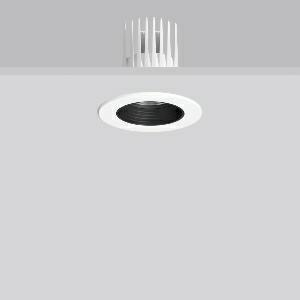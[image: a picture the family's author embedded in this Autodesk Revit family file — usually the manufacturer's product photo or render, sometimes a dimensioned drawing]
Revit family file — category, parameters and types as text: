
# Revit family: heledon_mini_e_901745_002_1_76_a57e
name_source: partatom
category: Lighting Fixtures
units: mm (PartAtom-declared; Revit-internal decimal feet)

## family parameters
Cut with Voids When Loaded = No
Host = Face
Light Source = No
Part Type = Normal
Room Calculation Point = No
Round Connector Dimension = Use Diameter
Shared = No

## types (1)
- HELEDON mini E (1 x LED Modul 940, 2150 lm, 4000)
    Apparent Load = 20 VA
    Approval mark = CE
    CIE Flux Codes = 98 100 100 100 100
    Color Rendering = 92
    Color Temperature = 4000
    Default Elevation = 1800 mm
    Description = Series: HELEDON mini
Round recessed downlight. Housing: die-cast aluminium, powder-coated. Black plastic ring and recessed LED to prevent glare from the side. Optical assembly with lens made of plastic (polycarbonate) for the best homogeneous light distribution - can be changed without tools. Best colour rendering index Ra>90. Suitable for Recessed ceiling mounting. Installation without tools thanks to spring fastening system. Including separate LED converter with connecting cable 600 mm.High quality converter without flickering and stroboscopic effect. Through-wiring box (5 pole) available as accessory. The following accessories can be mounted without use of tools: interchangeable lenses, decorative glasses, honeycomb louvre, clear and frosted diffusers, white interchangeable plastic ring. 
Colour: traffic white, matt (RAL 9016)
Diameter: 124 mm
Height: 3 mm
Cut-out diameter: 114 mm
Recess height: 170 mm
Luminaire: recess height: 120 mm
Lamp: LED
Socket: without socket
Colour temperature: 4000K
Colour rendering index (CRI): 92
System power: 20 W
Rated luminous flux: 2150 lm
Luminous efficiency: 108 lm/W
Control gear: Converter, dimmable, DALI
Protection class: II
Type of protection: IP 20
    Height = 0 mm  [stored 0 ft]
    Lamp = 1 x LED Modul 940
    Lamp Light Flux = 2150 lm
    Lamp count = 1
    Length = 124 mm  [stored 0.406824 ft]
    Lifetime = 50000 h
    Luminous efficacy = 108 lm/W
    Manufacturer = RZB
    ModVariant = No
    Model = 901745.002.1.76
    Mounting Place = Ceiling
    Mounting Type = Recessed
    Number of Poles = 1
    OnlyDefault = Yes
    Power Factor = 1
    Product Name = HELEDON mini E
    Product group = Recessed downlights
    ProductGroupID = 402
    Protection Class = Protection class II
    Protection Degree = IP 20
    RLX_Detail_Level = 1
    RLX_Emergency_Light_Flux = 0 lm
    RLX_Emergency_Type = 0
    RLX_Emergency_Type_DB = No
    RlxData = <blob elided: 124213 chars, md5=e70e0244>
    Socket = socket
    Standby Power = 0 W
    System Light Flux = 2150 lm
    System Power = 20 W
    Type Comments = Product without accessories
    Type Image = 901656.002.jpg
    URL = http://relux.com
    VarID = ---
    Voltage = 230 V
    Voltage Range = 220-240 V
    Weight = 0.00 kg
    Width = 0 mm  [stored 0 ft]

note: [stored X ft] marks values corroborated as IEEE doubles in the binary element streams (Revit-internal decimal feet)

## geometry (parser evidence)
native form markers: Blend x4, Sweep x12
no freeform markers — native parametric forms only
